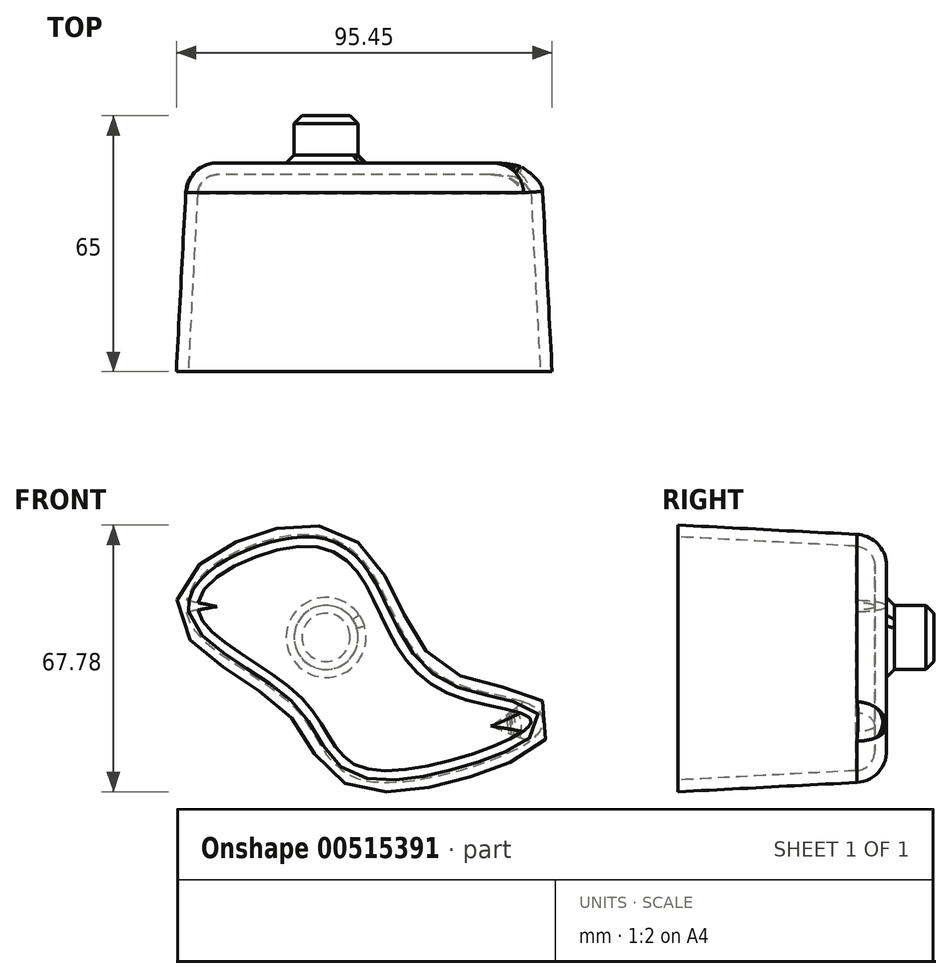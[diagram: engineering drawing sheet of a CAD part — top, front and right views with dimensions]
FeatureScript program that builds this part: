
annotation { "Feature Type Name" : "Feature", "Feature Type Description" : "" }
export const myFeature = defineFeature(function(context is Context, id is Id, definition is map)
    precondition{}
    {
        {
            var Q0;
            Q0=qCreatedBy(makeId("Front.planeOp"),FACE);
            var sketch = newSketch(context, id + "F0", { "sketchPlane" : qUnion([Q0])});
            skFitSpline(sketch, "E0", {"points": [v(-16.63, -23.64) * mm, v(-43.26, 0) * mm, v(-13.99, 14.64) * mm, v(1.94, -0.72) * mm, v(19.49, -22.45) * mm, v(40.9, -29.82) * mm, v(0, -41.44) * mm, v(-16.63, -23.64) * mm]});
            skSolve(sketch);
        }
        {
            var Q0;
            Q0 = qSketchRegion(id + "F0", true);
            var sketch = newSketch(context, id + "F1", { "sketchPlane" : qUnion([Q0])});
            skSolve(sketch);
        }
        {
            var Q0;
            Q0 = qSketchRegion(id + "F1", true);
            var Q1;
            Q1=makeQuery(id+"F1.imprint","IMPRINT",FACE,{"disambiguationData":[TD([[makeQuery(id+"F1.imprint","IMPRINT",EDGE,{"derivedFrom":makeQuery(id+"F0.imprint","IMPRINT",EDGE,{"derivedFrom":sQuery(id+"F0.wireOp",EDGE,"E0")})}),-1.0]])]});
            extrude(context, id + "F2", {"entities" : qUnion([Q0, Q1]), "depth" : 50 * mm, "offsetDistance" : 25.4 * mm, "hasDraft" : true, "draftAngle" : 3 * degree});
        }
        {
            var Q0;
            Q0=makeQuery(id+"F2.opExtrude","CAP_EDGE",EDGE,{"disambiguationData":[OSD([sQuery(id+"F0.wireOp",EDGE,"E0")])],"isStart":true});
            fillet(context, id + "F3", {"entities" : qUnion([Q0]), "radius" : 5 * mm, "tangentPropagation" : true, "allowEdgeOverflow" : false});
        }
        {
            var Q0;
            Q0=makeQuery(id+"F2.opExtrude","CAP_FACE",FACE,{"disambiguationData":[OSD([sQuery(id+"F0.wireOp",EDGE,"E0")])],"isStart":false});
            shell(context, id + "F4", {"entities" : qUnion([Q0]), "thickness" : 3 * mm, "oppositeDirection" : true});
        }
        {
            var Q0;
            Q0=makeQuery(id+"F2.opExtrude","CAP_FACE",FACE,{"disambiguationData":[OSD([sQuery(id+"F0.wireOp",EDGE,"E0")])],"isStart":true});
            var sketch = newSketch(context, id + "F5", { "sketchPlane" : qUnion([Q0])});
            skCircle(sketch, "E1", {"center": v(10.85, -8.2) * mm, "radius": 8.14 * mm});
            skSolve(sketch);
        }
        {
            var Q0;
            Q0=makeQuery(id+"F5.imprint","IMPRINT",FACE,{"disambiguationData":[TD([[makeQuery(id+"F5.imprint","IMPRINT",EDGE,{"derivedFrom":sQuery(id+"F5.wireOp",EDGE,"E1")}),1.0]])]});
            extrude(context, id + "F6", {"entities" : qUnion([Q0]), "operationType" : NewBodyOperationType.ADD, "depth" : 12 * mm, "offsetDistance" : 25.4 * mm});
        }
        {
            var Q0;
            Q0=makeQuery(id+"F6.opExtrude","CAP_FACE",FACE,{"disambiguationData":[OSD([sQuery(id+"F5.wireOp",EDGE,"E1")])],"isStart":false});
            var Q1;
            Q1=makeQuery(id+"F6.opExtrude","SWEPT_FACE",FACE,{"disambiguationData":[OSD([sQuery(id+"F5.wireOp",EDGE,"E1")])]});
            chamfer(context, id + "F7", {"entities" : qUnion([Q0, Q1]), "width" : 2 * mm, "tangentPropagation" : true});
        }
    });
